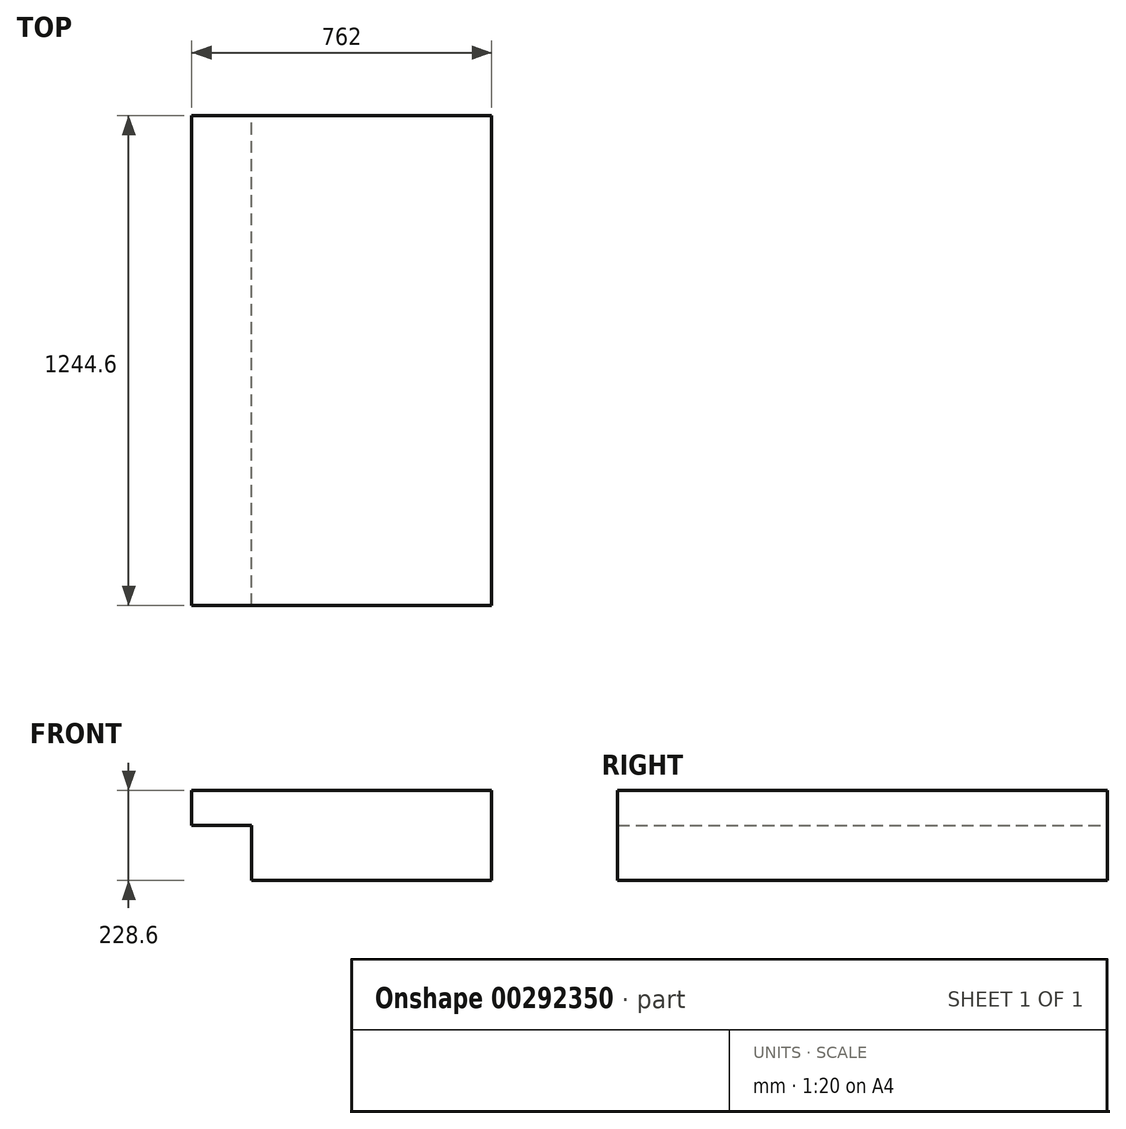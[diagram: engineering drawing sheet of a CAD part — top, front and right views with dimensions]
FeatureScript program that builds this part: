
annotation { "Feature Type Name" : "Feature", "Feature Type Description" : "" }
export const myFeature = defineFeature(function(context is Context, id is Id, definition is map)
    precondition{}
    {
        {
            var Q0;
            Q0=qCreatedBy(makeId("Top.planeOp"),FACE);
            var sketch = newSketch(context, id + "F0", { "sketchPlane" : qUnion([Q0])});
            skLineSegment(sketch, "E0.bottom", {"start": v(0, -622.3) * mm, "end": v(-762, -622.3) * mm});
            skLineSegment(sketch, "E0.top", {"start": v(0, 622.3) * mm, "end": v(-762, 622.3) * mm});
            skLineSegment(sketch, "E0.left", {"start": v(0, -622.3) * mm, "end": v(0, 622.3) * mm});
            skLineSegment(sketch, "E0.right", {"start": v(-762, -622.3) * mm, "end": v(-762, 622.3) * mm});
            skPoint(sketch, "E0.middle", {"position": v(-254, 0) * mm});
            skPoint(sketch, "E1.0", {"position": v(0, 0) * mm});
            skSolve(sketch);
        }
        {
            var Q0;
            Q0=qSketchRegion(id+"F0",true);
            extrude(context, id + "F1", {"entities" : qUnion([Q0]), "oppositeDirection" : true, "depth" : 228.6 * mm});
        }
        {
            var Q0;
            Q0=makeQuery(id+"F1.opExtrude","SWEPT_FACE",FACE,{"disambiguationData":[OSD([sQuery(id+"F0.wireOp",EDGE,"E0.right")])]});
            var sketch = newSketch(context, id + "F2", { "sketchPlane" : qUnion([Q0])});
            skLineSegment(sketch, "E2.bottom", {"start": v(622.3, -88.9) * mm, "end": v(-622.3, -88.9) * mm});
            skLineSegment(sketch, "E2.top", {"start": v(622.3, -228.6) * mm, "end": v(-622.3, -228.6) * mm});
            skLineSegment(sketch, "E2.left", {"start": v(622.3, -88.9) * mm, "end": v(622.3, -228.6) * mm});
            skLineSegment(sketch, "E2.right", {"start": v(-622.3, -88.9) * mm, "end": v(-622.3, -228.6) * mm});
            skSolve(sketch);
        }
        {
            var Q0;
            Q0 = qSketchRegion(id + "F2", true);
            extrude(context, id + "F3", {"entities" : qUnion([Q0]), "operationType" : NewBodyOperationType.REMOVE, "oppositeDirection" : true, "depth" : 152.4 * mm, "offsetDistance" : 25.4 * mm});
        }
    });
